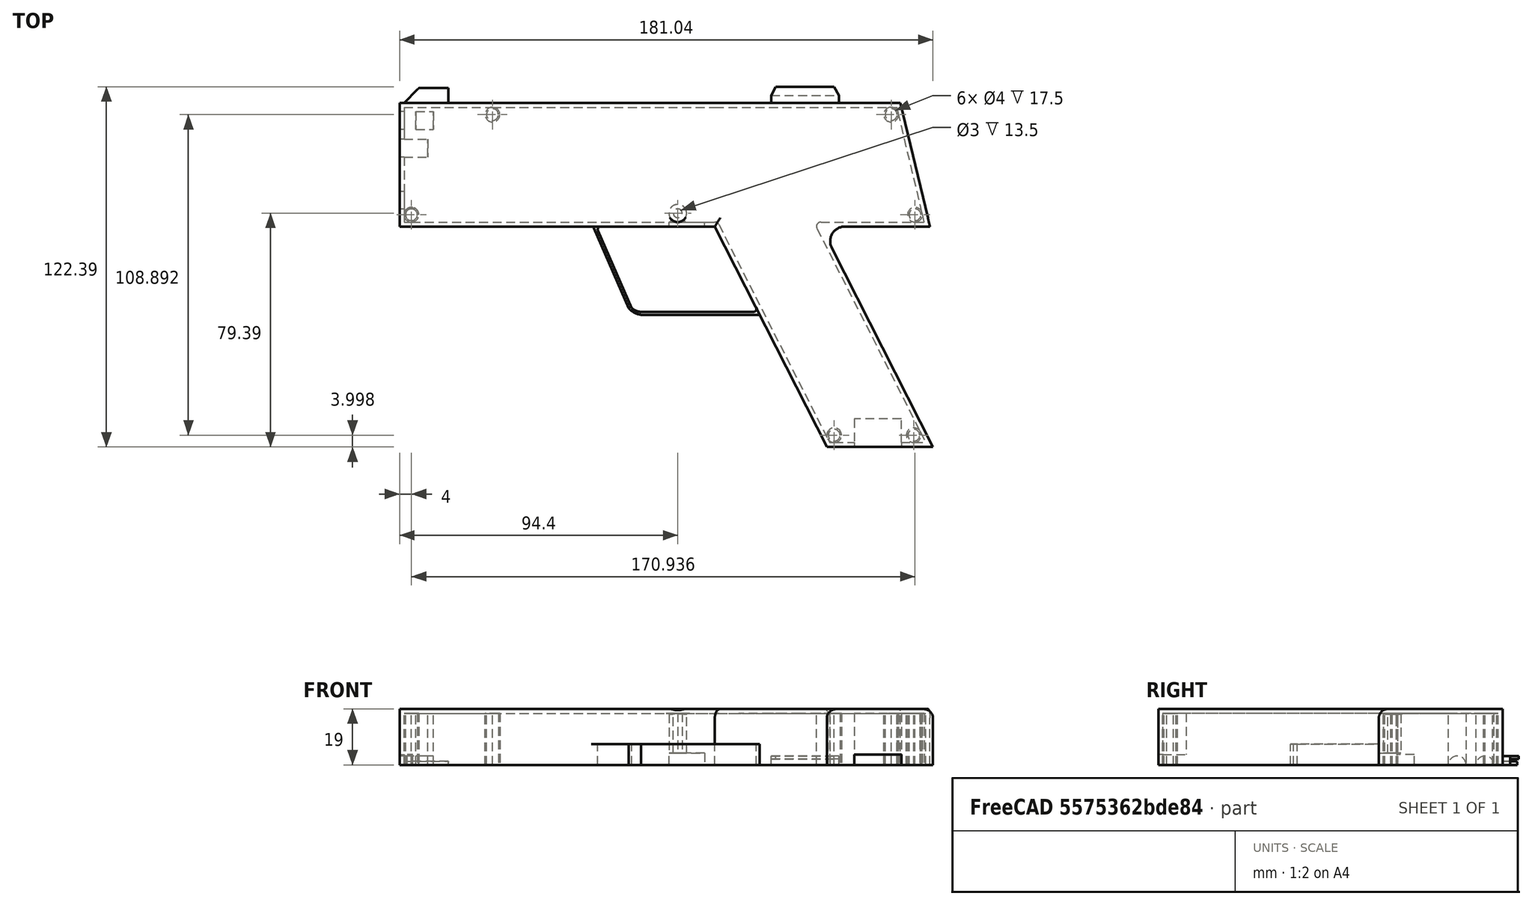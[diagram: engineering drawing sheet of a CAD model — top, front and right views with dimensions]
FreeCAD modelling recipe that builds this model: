
FCSTD DOCUMENT  (FreeCAD 0.21R33771 (Git))
Label: TaggerPart2
License: All rights reserved
LicenseURL: http://en.wikipedia.org/wiki/All_rights_reserved
objects: Sketcher::SketchObject×19, PartDesign::Pad×12, PartDesign::Fillet×5, PartDesign::Pocket×5, PartDesign::Thickness×1, PartDesign::Hole×1, App::MeasureDistance×1, PartDesign::Body×1, App::Part×1
note: 68 computed .brp shape members not serialized (recipe doc carries the construction recipe); baked Part::Feature solids carry a one-line shape summary decoded from their .brp

FEATURE [Sketcher::SketchObject] Sketch
  FullyConstrained = false
  MapMode = 5
  Support = -> [XY_Plane]
  sketch-geometry (12):
    g0: LineSegment StartX=0 StartY=0 StartZ=0 EndX=107 EndY=0 EndZ=0
    g1: LineSegment StartX=0 StartY=0 StartZ=0 EndX=0 EndY=-42 EndZ=0
    g2: LineSegment StartX=0 StartY=-42 StartZ=0 EndX=107 EndY=-42 EndZ=0
    g3: LineSegment StartX=107 StartY=0 StartZ=0 EndX=107 EndY=-42 EndZ=0
    g4: LineSegment StartX=107 StartY=0 StartZ=0 EndX=170 EndY=0 EndZ=0
    g5: LineSegment StartX=107 StartY=-42 StartZ=0 EndX=143 EndY=-42 EndZ=0
    g6: LineSegment StartX=107 StartY=-42 StartZ=0 EndX=145.042 EndY=-116.892 EndZ=0
    g7: LineSegment StartX=143 StartY=-42 StartZ=0 EndX=181.042 EndY=-116.892 EndZ=0
    g8: LineSegment StartX=145.042 StartY=-116.892 StartZ=0 EndX=181.042 EndY=-116.892 EndZ=0
    g9: LineSegment StartX=143 StartY=-42 StartZ=0 EndX=180 EndY=-42 EndZ=0
    g10: LineSegment StartX=180 StartY=-42 StartZ=0 EndX=170 EndY=0 EndZ=0
    g11: LineSegment StartX=170 StartY=0 StartZ=0 EndX=170 EndY=-42 EndZ=0
  constraints (32):
    c: Coincident(g0,g-1)
    c: PointOnObject(g0,g-1)
    c: Coincident(g1,g0)
    c: PointOnObject(g1,g-2)
    c: Coincident(g2,g1)
    c: Horizontal(g2)
    c: Coincident(g3,g0)
    c: Coincident(g3,g2)
    c: Vertical(g3)
    c: Coincident(g4,g0)
    c: PointOnObject(g4,g-1)
    c: Coincident(g5,g2)
    c: Horizontal(g5)
    c: Coincident(g6,g2)
    c: Coincident(g7,g5)
    c: Coincident(g8,g6)
    c: Coincident(g8,g7)
    c: Horizontal(g8)
    c: Coincident(g9,g7)
    c: Horizontal(g9)
    c: Coincident(g10,g9)
    c: Coincident(g10,g4)
    c: Coincident(g11,g4)
    c: PointOnObject(g11,g9)
    c: Vertical(g11)
    c: DistanceY(g1,g1) = 42
    c: DistanceX(g1,g9) = 180
    c: DistanceX(g0,g4) = 170
    c: Parallel(g7,g6)
    c: Distance(g7) = 84
    c: DistanceX(g5,g5) = 36
    c: DistanceX(g9,g9) = 37
FEATURE [Sketcher::SketchObject] Sketch001  label="Triggerumrahmung"
  ExternalGeometry = -> [Sketch]
  FullyConstrained = false
  MapMode = 5
  Support = -> [XY_Plane]
  sketch-geometry (16):
    g0: LineSegment StartX=107 StartY=-42 StartZ=0 EndX=107 EndY=-71 EndZ=0
    g1: LineSegment StartX=107 StartY=-71 StartZ=0 EndX=121.731 EndY=-71 EndZ=0
    g2: LineSegment StartX=107 StartY=-71 StartZ=0 EndX=66.7308 EndY=-71 EndZ=0
    g3: LineSegment StartX=66.7308 StartY=-71 StartZ=0 EndX=66.7308 EndY=-42 EndZ=0
    g4: LineSegment StartX=121.731 StartY=-71 StartZ=0 EndX=81.9929 EndY=-71 EndZ=0
    g5: LineSegment StartX=78.7821 StartY=-69.7248 StartZ=0 EndX=66.7308 EndY=-42 EndZ=0
    g6: ArcOfCircle CenterX=82.1691 CenterY=-65.8766 CenterZ=0 NormalX=0 NormalY=0 NormalZ=1 AngleXU=0 Radius=5.12641 StartAngle=3.99065 EndAngle=4.678
    g7: LineSegment StartX=121.731 StartY=-71 StartZ=0 EndX=121.731 EndY=-72 EndZ=0
    g8: LineSegment StartX=121.731 StartY=-72 StartZ=0 EndX=81.9929 EndY=-72 EndZ=0
    g9: LineSegment StartX=81.9929 StartY=-71 StartZ=0 EndX=81.9929 EndY=-72 EndZ=0
    g10: ArcOfCircle CenterX=82.7291 CenterY=-65.6034 CenterZ=0 NormalX=0 NormalY=0 NormalZ=1 AngleXU=0 Radius=6.43882 StartAngle=3.8362 EndAngle=4.59779
    g11: LineSegment StartX=66.7308 StartY=-42 StartZ=0 EndX=65.7308 EndY=-42 EndZ=0
    g12: LineSegment StartX=65.7308 StartY=-42 StartZ=0 EndX=77.7821 EndY=-69.7248 EndZ=0
    g13: LineSegment StartX=78.7821 StartY=-69.7248 StartZ=0 EndX=77.7821 EndY=-69.7248 EndZ=0
    g14: LineSegment StartX=121.731 StartY=-72 StartZ=0 EndX=122.239 EndY=-72 EndZ=0
    g15: LineSegment StartX=122.239 StartY=-72 StartZ=0 EndX=121.731 EndY=-71 EndZ=0
  constraints (44):
    c: Coincident(g0,g-4)
    c: Vertical(g0)
    c: DistanceY(g0,g0) = 29
    c: PointOnObject(g1,g-3)
    c: Horizontal(g1)
    c: Coincident(g1,g0)
    c: Coincident(g2,g0)
    c: Horizontal(g2)
    c: DistanceX(g2,g1) = 55
    c: Coincident(g3,g2)
    c: PointOnObject(g3,g-4)
    c: Vertical(g3)
    c: Coincident(g4,g1)
    c: Coincident(g5,g3)
    c: Horizontal(g4)
    c: Coincident(g6,g5)
    c: Coincident(g6,g4)
    c: Coincident(g7,g4)
    c: Vertical(g7)
    c: Coincident(g8,g7)
    c: Horizontal(g8)
    c: Coincident(g9,g4)
    c: Coincident(g9,g8)
    c: Vertical(g9)
    c: DistanceY(g9,g9) = 1
    c: Coincident(g10,g8)
    c: Coincident(g11,g5)
    c: PointOnObject(g11,g-4)
    c: DistanceX(g11,g11) = 1
    c: Coincident(g12,g11)
    c: Coincident(g12,g10)
    c: DistanceX(g6) = 82.1691
    c: DistanceY(g6) = -65.8766
    c: Equal(g12,g5)
    c: Coincident(g13,g5)
    c: Horizontal(g13)
    c: Coincident(g10,g13)
    c: DistanceX(g4) = 81.9929
    c: DistanceX(g5) = 78.7821
    c: Coincident(g14,g8)
    c: PointOnObject(g14,g-3)
    c: Horizontal(g14)
    c: Coincident(g15,g14)
    c: Coincident(g15,g4)
FEATURE [Sketcher::SketchObject] Sketch002  label="Kim2"
  AttachmentOffset = pos=(0,0,2) rot=(0,0,1;0rad)
  ExternalGeometry = -> [Sketch]
  FullyConstrained = false
  MapMode = 5
  Placement = pos=(0,0,2) rot=(0,0,1;0rad)
  Support = -> [XY_Plane]
  sketch-geometry (10):
    g0: LineSegment StartX=170 StartY=0 StartZ=0 EndX=170 EndY=-42 EndZ=0
    g1: LineSegment StartX=149.115 StartY=0 StartZ=0 EndX=149.115 EndY=2.5 EndZ=0
    g2: LineSegment StartX=149.115 StartY=2.5 StartZ=0 EndX=147.523 EndY=5.5 EndZ=0
    g3: LineSegment StartX=147.523 StartY=5.5 StartZ=0 EndX=127.662 EndY=5.5 EndZ=0
    g4: LineSegment StartX=127.662 StartY=5.5 StartZ=0 EndX=126.07 EndY=2.5 EndZ=0
    g5: LineSegment StartX=126.07 StartY=2.5 StartZ=0 EndX=126.07 EndY=0 EndZ=0
    g6: LineSegment StartX=126.07 StartY=2.5 StartZ=0 EndX=149.115 EndY=2.5 EndZ=0
    g7: LineSegment StartX=127.662 StartY=5.5 StartZ=0 EndX=127.662 EndY=2.5 EndZ=0
    g8: LineSegment StartX=147.523 StartY=5.5 StartZ=0 EndX=147.523 EndY=2.5 EndZ=0
    g9: LineSegment StartX=126.07 StartY=0 StartZ=0 EndX=149.115 EndY=0 EndZ=0
  constraints (26):
    c: Coincident(g0,g-6)
    c: PointOnObject(g0,g-7)
    c: Vertical(g0)
    c: PointOnObject(g1,g-4)
    c: Vertical(g1)
    c: Coincident(g3,g2)
    c: Horizontal(g3)
    c: Coincident(g4,g3)
    c: Coincident(g5,g4)
    c: PointOnObject(g5,g-4)
    c: Equal(g5,g1)
    c: Equal(g4,g2)
    c: Coincident(g2,g1)
    c: Vertical(g5)
    c: Coincident(g6,g4)
    c: Coincident(g6,g1)
    c: Coincident(g7,g3)
    c: PointOnObject(g7,g6)
    c: Vertical(g7)
    c: Coincident(g8,g2)
    c: PointOnObject(g8,g6)
    c: Vertical(g8)
    c: DistanceY(g8,g8) = 3
    c: DistanceY(g5,g3) = 5.5
    c: Coincident(g9,g5)
    c: Coincident(g9,g1)
FEATURE [Sketcher::SketchObject] Sketch003  label="Korn"
  ExternalGeometry = -> [Sketch,Sketch002]
  FullyConstrained = false
  MapMode = 5
  Support = -> [XY_Plane]
  sketch-geometry (7):
    g0: LineSegment StartX=1.52333 StartY=0 StartZ=0 EndX=6.52333 EndY=5 EndZ=0
    g1: LineSegment StartX=6.52333 StartY=5 StartZ=0 EndX=16.5233 EndY=5 EndZ=0
    g2: LineSegment StartX=16.5233 StartY=5 StartZ=0 EndX=16.5233 EndY=0 EndZ=0
    g3: LineSegment StartX=16.5233 StartY=0 StartZ=0 EndX=1.52333 EndY=0 EndZ=0
    g4: LineSegment StartX=127.662 StartY=5.5 StartZ=0 EndX=127.662 EndY=0 EndZ=0
    g5: LineSegment StartX=6.52333 StartY=5 StartZ=0 EndX=6.52333 EndY=0 EndZ=0
    g6: LineSegment StartX=1.52333 StartY=0 StartZ=0 EndX=1.52333 EndY=-1.50251 EndZ=0
  constraints (19):
    c: Coincident(g1,g0)
    c: Horizontal(g1)
    c: Coincident(g2,g1)
    c: PointOnObject(g2,g-3)
    c: Coincident(g3,g2)
    c: Coincident(g3,g0)
    c: Vertical(g2)
    c: Coincident(g4,g-6)
    c: PointOnObject(g4,g-8)
    c: Vertical(g4)
    c: DistanceY(g2,g2) = 5
    c: Coincident(g5,g0)
    c: PointOnObject(g5,g3)
    c: Vertical(g5)
    c: Angle(g0,g5) = 0.785398
    c: DistanceX(g3,g3) = 15
    c: PointOnObject(g0,g-3)
    c: Coincident(g6,g0)
    c: Vertical(g6)
FEATURE [PartDesign::Pad] Pad
  Direction = (0,0,1)
  Length = 19
  Length2 = 10
  Profile = -> Sketch
  ReferenceAxis = -> Sketch [N_Axis]
  Type = 0
FEATURE [PartDesign::Thickness] Thickness
  Base = -> Pad [Face10]
  BaseFeature = -> Pad
  Intersection = false
  Join = 0
  Mode = 0
  Reversed = true
  SupportTransform = false
  Value = 1.5
FEATURE [Sketcher::SketchObject] Sketch004  label="Kim1"
  ExternalGeometry = -> [Sketch002]
  FullyConstrained = true
  MapMode = 5
  Support = -> [XY_Plane]
  sketch-geometry (4):
    g0: LineSegment StartX=126.07 StartY=2.5 StartZ=0 EndX=149.115 EndY=2.5 EndZ=0
    g1: LineSegment StartX=149.115 StartY=2.5 StartZ=0 EndX=149.115 EndY=0 EndZ=0
    g2: LineSegment StartX=149.115 StartY=0 StartZ=0 EndX=126.07 EndY=0 EndZ=0
    g3: LineSegment StartX=126.07 StartY=0 StartZ=0 EndX=126.07 EndY=2.5 EndZ=0
  constraints (8):
    c: Coincident(g0,g-5)
    c: Coincident(g0,g-7)
    c: Coincident(g1,g0)
    c: Coincident(g1,g-8)
    c: Coincident(g2,g-8)
    c: Coincident(g3,g0)
    c: Coincident(g2,g1)
    c: Coincident(g3,g2)
FEATURE [PartDesign::Pad] Pad001
  BaseFeature = -> Thickness
  Direction = (0,0,1)
  Length = 2
  Length2 = 10
  Profile = -> Sketch004
  ReferenceAxis = -> Sketch004 [N_Axis]
  Type = 0
FEATURE [PartDesign::Pad] Pad002
  BaseFeature = -> Pad001
  Direction = (0,0,1)
  Length = 1
  Length2 = 10
  Profile = -> Sketch002
  ReferenceAxis = -> Sketch002 [N_Axis]
  Type = 0
FEATURE [PartDesign::Pad] Pad003
  BaseFeature = -> Pad002
  Direction = (0,0,1)
  Length = 1.2
  Length2 = 10
  Profile = -> Sketch003
  ReferenceAxis = -> Sketch003 [N_Axis]
  Type = 0
FEATURE [PartDesign::Fillet] Fillet
  Base = -> Pad003 [Edge93]
  BaseFeature = -> Pad003
  Radius = 0.5
  SupportTransform = false
  UseAllEdges = false
FEATURE [PartDesign::Pad] Pad004
  BaseFeature = -> Fillet
  Direction = (0,0,1)
  Length = 7
  Length2 = 10
  Profile = -> Sketch001
  ReferenceAxis = -> Sketch001 [N_Axis]
  Type = 0
FEATURE [Sketcher::SketchObject] Sketch005  label="laserlöcher"
  ExternalGeometry = -> [Pad004]
  FullyConstrained = true
  MapMode = 5
  Placement = pos=(1.5,0,0) rot=(0.57735,0.57735,0.57735;2.0944rad)
  Support = -> [Pad004]
  sketch-geometry (6):
    g0: LineSegment StartX=-12.3 StartY=0 StartZ=0 EndX=0 EndY=0 EndZ=0
    g1: ArcOfCircle CenterX=-15.4 CenterY=0 CenterZ=0 NormalX=0 NormalY=0 NormalZ=1 AngleXU=0 Radius=3.1 StartAngle=0 EndAngle=3.14159
    g2: LineSegment StartX=-18.5 StartY=0 StartZ=0 EndX=-12.3 EndY=0 EndZ=0
    g3: ArcOfCircle CenterX=-6 CenterY=0 CenterZ=0 NormalX=0 NormalY=0 NormalZ=1 AngleXU=0 Radius=3.3 StartAngle=0 EndAngle=3.14159
    g4: LineSegment StartX=-9.3 StartY=0 StartZ=0 EndX=-2.7 EndY=0 EndZ=0
    g5: LineSegment StartX=-40.5 StartY=0 StartZ=0 EndX=-18.5 EndY=0 EndZ=0
  constraints (18):
    c: Radius(g1) = 3.1
    c: Coincident(g2,g1)
    c: Coincident(g2,g1)
    c: Coincident(g0,g-1)
    c: PointOnObject(g3,g0)
    c: PointOnObject(g3,g0)
    c: PointOnObject(g3,g0)
    c: Radius(g3) = 3.3
    c: Coincident(g4,g3)
    c: Coincident(g4,g3)
    c: DistanceX(g1,g3) = 3
    c: Coincident(g5,g-3)
    c: Coincident(g5,g1)
    c: Horizontal(g5)
    c: DistanceX(g5,g5) = 22
    c: Coincident(g0,g1)
    c: Horizontal(g0)
    c: PointOnObject(g1,g2)
FEATURE [Sketcher::SketchObject] Sketch006  label="Schraubenlöcher"
  ExternalGeometry = -> [Pad004]
  FullyConstrained = false
  MapMode = 5
  Placement = pos=(0,0,17.5) rot=(1,0,0;3.14159rad)
  Support = -> [Pad004]
  sketch-geometry (20):
    g0: Circle CenterX=31.5 CenterY=4 CenterZ=0 NormalX=0 NormalY=0 NormalZ=1 AngleXU=0 Radius=2
    g1: Circle CenterX=31.5 CenterY=4 CenterZ=0 NormalX=0 NormalY=0 NormalZ=1 AngleXU=0 Radius=2.5
    g2: Circle CenterX=4 CenterY=38 CenterZ=0 NormalX=0 NormalY=0 NormalZ=1 AngleXU=0 Radius=2.5
    g3: Circle CenterX=4 CenterY=38 CenterZ=0 NormalX=0 NormalY=0 NormalZ=1 AngleXU=0 Radius=2
    g4: Circle CenterX=147.497 CenterY=112.892 CenterZ=0 NormalX=0 NormalY=0 NormalZ=1 AngleXU=0 Radius=2
    g5: Circle CenterX=147.497 CenterY=112.892 CenterZ=0 NormalX=0 NormalY=0 NormalZ=1 AngleXU=0 Radius=2.5
    g6: Circle CenterX=166.841 CenterY=4 CenterZ=0 NormalX=0 NormalY=0 NormalZ=1 AngleXU=0 Radius=2
    g7: Circle CenterX=166.841 CenterY=4 CenterZ=0 NormalX=0 NormalY=0 NormalZ=1 AngleXU=0 Radius=2.5
    g8: Circle CenterX=174.524 CenterY=112.892 CenterZ=0 NormalX=0 NormalY=0 NormalZ=1 AngleXU=0 Radius=2
    g9: Circle CenterX=174.524 CenterY=112.892 CenterZ=0 NormalX=0 NormalY=0 NormalZ=1 AngleXU=0 Radius=2.5
    g10: Circle CenterX=174.936 CenterY=38 CenterZ=0 NormalX=0 NormalY=0 NormalZ=1 AngleXU=0 Radius=2
    g11: Circle CenterX=174.936 CenterY=38 CenterZ=0 NormalX=0 NormalY=0 NormalZ=1 AngleXU=0 Radius=2.5
    g12: GeomPoint X=166.841 Y=1.5 Z=0
    g13: GeomPoint X=169.273 Y=3.42095 Z=0
    g14: GeomPoint X=174.936 Y=40.5 Z=0
    g15: GeomPoint X=177.368 Y=37.4209 Z=0
    g16: GeomPoint X=147.497 Y=115.392 Z=0
    g17: GeomPoint X=145.268 Y=114.024 Z=0
    g18: GeomPoint X=31.5 Y=1.5 Z=0
    g19: GeomPoint X=1.5 Y=3.78568 Z=0
  constraints (39):
    c: Coincident(g1,g0)
    c: Coincident(g3,g2)
    c: Equal(g3,g0)
    c: Tangent(g-5,g2)
    c: Tangent(g2,g-6)
    c: Radius(g2) = 2.5
    c: Radius(g3) = 2
    c: Coincident(g5,g4)
    c: Radius(g5) = 2.5
    c: Radius(g4) = 2
    c: Coincident(g7,g6)
    c: Radius(g6) = 2
    c: Coincident(g9,g8)
    c: Radius(g8) = 2
    c: Radius(g9) = 2.5
    c: Tangent(g9,g-8)
    c: Tangent(g9,g-7)
    c: Coincident(g11,g10)
    c: Radius(g11) = 2.5
    c: Radius(g7) = 2.5
    c: PointOnObject(g12,g7)
    c: PointOnObject(g13,g7)
    c: PointOnObject(g12,g-9)
    c: PointOnObject(g13,g-3)
    c: Radius(g10) = 2
    c: PointOnObject(g14,g11)
    c: PointOnObject(g15,g11)
    c: PointOnObject(g14,g-10)
    c: PointOnObject(g15,g-3)
    c: Radius(g1) = 2.5
    c: PointOnObject(g16,g5)
    c: PointOnObject(g17,g5)
    c: PointOnObject(g16,g-8)
    c: PointOnObject(g17,g-11)
    c: PointOnObject(g18,g1)
    c: PointOnObject(g18,g-4)
    c: DistanceX(g-6,g-6) = 0
    c: PointOnObject(g19,g-6)
    c: DistanceX(g19,g0) = 30
FEATURE [PartDesign::Pad] Pad005
  BaseFeature = -> Pad004
  Direction = (0,0,-1)
  Length = 17.5
  Length2 = 10
  Profile = -> Sketch006
  ReferenceAxis = -> Sketch006 [N_Axis]
  Type = 0
FEATURE [Sketcher::SketchObject] Sketch007  label="Triggerausschnitt"
  ExternalGeometry = -> [Pad005]
  FullyConstrained = true
  MapMode = 5
  Placement = pos=(0,-42,0) rot=(1,0,0;1.5708rad)
  Support = -> [Pad005]
  sketch-geometry (4):
    g0: LineSegment StartX=103.5 StartY=0 StartZ=0 EndX=103.5 EndY=4 EndZ=0
    g1: LineSegment StartX=103.5 StartY=4 StartZ=0 EndX=91.5 EndY=4 EndZ=0
    g2: LineSegment StartX=91.5 StartY=4 StartZ=0 EndX=91.5 EndY=0 EndZ=0
    g3: LineSegment StartX=91.5 StartY=0 StartZ=0 EndX=103.5 EndY=0 EndZ=0
  constraints (12):
    c: PointOnObject(g0,g-3)
    c: Vertical(g0)
    c: Coincident(g1,g0)
    c: Horizontal(g1)
    c: Coincident(g2,g1)
    c: PointOnObject(g2,g-3)
    c: Vertical(g2)
    c: DistanceY(g2,g2) = 4
    c: Coincident(g3,g2)
    c: Coincident(g3,g0)
    c: DistanceX(g1,g0) = 12
    c: DistanceX(g0,g-3) = 3.5
FEATURE [PartDesign::Pocket] Pocket
  BaseFeature = -> Pad005
  Direction = (0,1,-2e-16)
  Length = 5
  Length2 = 5
  Profile = -> Sketch007
  ReferenceAxis = -> Sketch007 [N_Axis]
  Type = 0
FEATURE [PartDesign::Hole] Hole
  BaseFeature = -> Pocket
  CustomThreadClearance = 0
  Depth = 25
  DepthType = 0
  Diameter = 6
  DrillForDepth = false
  DrillPoint = 1
  DrillPointAngle = 118
  HoleCutCountersinkAngle = 90
  HoleCutCustomValues = false
  HoleCutDepth = 0
  HoleCutDiameter = 6.1
  HoleCutType = 0
  ModelThread = false
  Profile = -> Sketch005
  Tapered = false
  TaperedAngle = 90
  ThreadClass = 0
  ThreadDepth = 25
  ThreadDepthType = 0
  ThreadDirection = 0
  ThreadFit = 0
  ThreadSize = 0
  ThreadType = 0
  Threaded = false
  UseCustomThreadClearance = false
FEATURE [Sketcher::SketchObject] Sketch010  label="Datenkabelloch"
  FullyConstrained = false
  MapMode = 5
  Placement = pos=(0,-115.392,0) rot=(0,0.707107,0.707107;3.14159rad)
  sketch-geometry (10):
    g0: LineSegment StartX=-178.598 StartY=11.5 StartZ=0 EndX=-174.524 EndY=11.5 EndZ=0
    g1: LineSegment StartX=-147.497 StartY=11.5 StartZ=0 EndX=-145.963 EndY=11.5 EndZ=0
    g2: LineSegment StartX=-178.598 StartY=0 StartZ=0 EndX=-162.28 EndY=0 EndZ=0
    g3: LineSegment StartX=-162.28 StartY=0 StartZ=0 EndX=-145.963 EndY=0 EndZ=0
    g4: LineSegment StartX=-162.28 StartY=0 StartZ=0 EndX=-162.28 EndY=3.5 EndZ=0
    g5: LineSegment StartX=-162.28 StartY=3.5 StartZ=0 EndX=-154.28 EndY=3.5 EndZ=0
    g6: LineSegment StartX=-162.28 StartY=3.5 StartZ=0 EndX=-170.28 EndY=3.5 EndZ=0
    g7: LineSegment StartX=-170.28 StartY=3.5 StartZ=0 EndX=-170.28 EndY=3.73e-14 EndZ=0
    g8: LineSegment StartX=-154.28 StartY=3.5 StartZ=0 EndX=-154.28 EndY=-3.86e-14 EndZ=0
    g9: LineSegment StartX=-154.28 StartY=-3.86e-14 StartZ=0 EndX=-170.28 EndY=3.74e-14 EndZ=0
  constraints (19):
    c: Coincident(g3,g2)
    c: Equal(g2,g3)
    c: Coincident(g4,g2)
    c: Vertical(g4)
    c: DistanceY(g4,g4) = 3.5
    c: Coincident(g5,g4)
    c: Horizontal(g5)
    c: Coincident(g6,g5)
    c: Equal(g6,g5)
    c: Horizontal(g6)
    c: DistanceX(g5,g5) = 8
    c: Coincident(g7,g6)
    c: PointOnObject(g7,g2)
    c: Vertical(g7)
    c: Coincident(g8,g5)
    c: PointOnObject(g8,g3)
    c: Vertical(g8)
    c: Coincident(g9,g8)
    c: Coincident(g9,g7)
FEATURE [PartDesign::Pocket] Pocket001
  BaseFeature = -> Hole
  Direction = (0,-1,2e-16)
  Length = 5
  Length2 = 5
  Profile = -> Sketch010
  ReferenceAxis = -> Sketch010 [N_Axis]
  Type = 0
FEATURE [Sketcher::SketchObject] Sketch011  label="Lautsprecherbefestigung"
  ExternalGeometry = -> [Pocket001]
  FullyConstrained = false
  MapMode = 5
  Placement = pos=(0,0,17.5) rot=(1,0,0;3.14159rad)
  Support = -> [Pocket001]
  sketch-geometry (7):
    g0: Circle CenterX=131.056 CenterY=21.3061 CenterZ=0 NormalX=0 NormalY=0 NormalZ=1 AngleXU=0 Radius=15.5
    g1: Circle CenterX=131.056 CenterY=21.3061 CenterZ=0 NormalX=0 NormalY=0 NormalZ=1 AngleXU=0 Radius=16
    g2: LineSegment StartX=131.056 StartY=21.3061 StartZ=0 EndX=131.056 EndY=1.5 EndZ=0
    g3: LineSegment StartX=131.056 StartY=21.3061 StartZ=0 EndX=143 EndY=40.5 EndZ=0
    g4: LineSegment StartX=143 StartY=42 StartZ=0 EndX=131.056 EndY=21.3061 EndZ=0
    g5: LineSegment StartX=141.678 StartY=42.7087 StartZ=0 EndX=131.056 EndY=21.3061 EndZ=0
    g6: LineSegment StartX=131.056 StartY=21.3061 StartZ=0 EndX=147.497 EndY=112.892 EndZ=0
  constraints (14):
    c: Coincident(g1,g0)
    c: Radius(g1) = 16
    c: Radius(g0) = 15.5
    c: Coincident(g2,g0)
    c: PointOnObject(g2,g-3)
    c: Vertical(g2)
    c: Coincident(g3,g0)
    c: Coincident(g3,g-8)
    c: Coincident(g4,g0)
    c: Coincident(g5,g0)
    c: Equal(g5,g4)
    c: Coincident(g6,g0)
    c: DistanceX(g0) = 131.056
    c: DistanceY(g0) = 21.3061
FEATURE [Sketcher::SketchObject] Sketch012  label="Lautsprecherbefestigung-optimierungen"
  ExternalGeometry = -> [Sketch011]
  FullyConstrained = true
  MapMode = 5
  Placement = pos=(0,0,17.5) rot=(1,0,0;3.14159rad)
  Support = -> [Pocket001]
  sketch-geometry (21):
    g0: ArcOfCircle CenterX=131.056 CenterY=21.3061 CenterZ=0 NormalX=0 NormalY=0 NormalZ=1 AngleXU=0 Radius=15.5 StartAngle=1.24234 EndAngle=1.89925
    g1: LineSegment StartX=126.056 StartY=35.9775 StartZ=0 EndX=131.056 EndY=35.9775 EndZ=0
    g2: LineSegment StartX=131.056 StartY=35.9775 StartZ=0 EndX=136.056 EndY=35.9775 EndZ=0
    g3: LineSegment StartX=131.056 StartY=35.9775 StartZ=0 EndX=131.056 EndY=21.3061 EndZ=0
    g4: LineSegment StartX=126.056 StartY=35.9775 StartZ=0 EndX=126.056 EndY=36.5048 EndZ=0
    g5: LineSegment StartX=136.056 StartY=35.9775 StartZ=0 EndX=136.056 EndY=36.5048 EndZ=0
    g6: ArcOfCircle CenterX=131.056 CenterY=21.3061 CenterZ=0 NormalX=0 NormalY=0 NormalZ=1 AngleXU=0 Radius=16 StartAngle=1.25297 EndAngle=1.88862
    g7: ArcOfCircle CenterX=131.056 CenterY=21.3061 CenterZ=0 NormalX=0 NormalY=0 NormalZ=1 AngleXU=0 Radius=15.5 StartAngle=4.38393 EndAngle=5.04084
    g8: LineSegment StartX=126.056 StartY=6.63469 StartZ=0 EndX=131.056 EndY=6.63469 EndZ=0
    g9: LineSegment StartX=131.056 StartY=6.63469 StartZ=0 EndX=136.056 EndY=6.63469 EndZ=0
    g10: LineSegment StartX=126.056 StartY=6.63469 StartZ=0 EndX=126.056 EndY=6.10741 EndZ=0
    g11: LineSegment StartX=136.056 StartY=6.63469 StartZ=0 EndX=136.056 EndY=6.10741 EndZ=0
    g12: ArcOfCircle CenterX=131.056 CenterY=21.3061 CenterZ=0 NormalX=0 NormalY=0 NormalZ=1 AngleXU=0 Radius=16 StartAngle=4.39457 EndAngle=5.03021
    g13: LineSegment StartX=131.056 StartY=6.63469 StartZ=0 EndX=131.056 EndY=21.3061 EndZ=0
    g14: ArcOfCircle CenterX=131.056 CenterY=21.3061 CenterZ=0 NormalX=0 NormalY=0 NormalZ=1 AngleXU=0 Radius=15.5 StartAngle=3.05115 EndAngle=3.23204
    g15: LineSegment StartX=115.619 StartY=22.7061 StartZ=0 EndX=115.619 EndY=21.3061 EndZ=0
    g16: LineSegment StartX=115.619 StartY=21.3061 StartZ=0 EndX=115.619 EndY=19.9061 EndZ=0
    g17: LineSegment StartX=115.619 StartY=21.3061 StartZ=0 EndX=131.056 EndY=21.3061 EndZ=0
    g18: LineSegment StartX=115.619 StartY=22.7061 StartZ=0 EndX=115.117 EndY=22.7061 EndZ=0
    g19: LineSegment StartX=115.619 StartY=19.9061 StartZ=0 EndX=115.117 EndY=19.9061 EndZ=0
    g20: ArcOfCircle CenterX=131.056 CenterY=21.3061 CenterZ=0 NormalX=0 NormalY=0 NormalZ=1 AngleXU=0 Radius=16 StartAngle=3.05398 EndAngle=3.2292
  constraints (57):
    c: Coincident(g6,g5)
    c: Coincident(g0,g5)
    c: Vertical(g5)
    c: Vertical(g4)
    c: Coincident(g6,g4)
    c: Coincident(g4,g0)
    c: Coincident(g2,g1)
    c: Coincident(g1,g3)
    c: Horizontal(g1)
    c: Horizontal(g2)
    c: Vertical(g3)
    c: DistanceX(g2,g2) = 5
    c: Coincident(g1,g0)
    c: PointOnObject(g5,g-3)
    c: Coincident(g6,g-4)
    c: Coincident(g6,g3)
    c: Coincident(g6,g0)
    c: Coincident(g0,g2)
    c: PointOnObject(g0,g-4)
    c: Coincident(g7,g0)
    c: PointOnObject(g7,g-4)
    c: Coincident(g8,g7)
    c: Horizontal(g8)
    c: Coincident(g9,g8)
    c: Coincident(g9,g7)
    c: Horizontal(g9)
    c: Equal(g9,g8)
    c: DistanceX(g8,g8) = 5
    c: Coincident(g10,g7)
    c: PointOnObject(g10,g-3)
    c: Vertical(g10)
    c: Coincident(g11,g7)
    c: Coincident(g12,g0)
    c: Coincident(g12,g10)
    c: Coincident(g12,g11)
    c: Coincident(g13,g8)
    c: Coincident(g13,g0)
    c: Coincident(g14,g0)
    c: PointOnObject(g14,g-4)
    c: Coincident(g15,g14)
    c: Vertical(g15)
    c: Coincident(g16,g15)
    c: Coincident(g16,g14)
    c: Vertical(g16)
    c: Vertical(g11)
    c: Equal(g16,g15)
    c: Coincident(g17,g15)
    c: Coincident(g17,g0)
    c: Coincident(g18,g14)
    c: PointOnObject(g18,g-3)
    c: Horizontal(g18)
    c: Coincident(g19,g14)
    c: Horizontal(g19)
    c: Coincident(g20,g0)
    c: Coincident(g20,g19)
    c: Coincident(g20,g18)
    c: DistanceY(g15,g15) = 1.4
FEATURE [Sketcher::SketchObject] Sketch013  label="Sechsecke-Loch"
  ExternalGeometry = -> [Sketch011,Sketch012]
  FullyConstrained = true
  MapMode = 5
  Placement = pos=(0,0,17.5) rot=(1,0,0;3.14159rad)
  Support = -> [Pocket001]
  sketch-geometry (65):
    g0: LineSegment StartX=131.056 StartY=21.3061 StartZ=0 EndX=131.056 EndY=23.3061 EndZ=0
    g1: LineSegment StartX=131.056 StartY=21.3061 StartZ=0 EndX=131.056 EndY=19.3061 EndZ=0
    g2: LineSegment StartX=131.056 StartY=23.3061 StartZ=0 EndX=132.21 EndY=23.3061 EndZ=0
    g3: LineSegment StartX=131.056 StartY=23.3061 StartZ=0 EndX=129.901 EndY=23.3061 EndZ=0
    g4: LineSegment StartX=129.901 StartY=23.3061 StartZ=0 EndX=128.746 EndY=21.3061 EndZ=0
    g5: LineSegment StartX=131.056 StartY=19.3061 StartZ=0 EndX=132.21 EndY=19.3061 EndZ=0
    g6: LineSegment StartX=131.056 StartY=19.3061 StartZ=0 EndX=129.901 EndY=19.3061 EndZ=0
    g7: LineSegment StartX=129.901 StartY=19.3061 StartZ=0 EndX=128.746 EndY=21.3061 EndZ=0
    g8: LineSegment StartX=132.21 StartY=19.3061 StartZ=0 EndX=133.365 EndY=21.3061 EndZ=0
    g9: LineSegment StartX=133.365 StartY=21.3061 StartZ=0 EndX=132.21 EndY=23.3061 EndZ=0
    g10: LineSegment StartX=129.901 StartY=19.3061 StartZ=0 EndX=132.21 EndY=19.3061 EndZ=0
    g11: LineSegment StartX=129.901 StartY=19.3061 StartZ=0 EndX=129.151 EndY=18.0071 EndZ=0
    g12: LineSegment StartX=132.21 StartY=19.3061 StartZ=0 EndX=132.96 EndY=18.0071 EndZ=0
    g13: LineSegment StartX=133.365 StartY=21.3061 StartZ=0 EndX=134.865 EndY=21.3061 EndZ=0
    g14: LineSegment StartX=132.21 StartY=23.3061 StartZ=0 EndX=132.96 EndY=24.6051 EndZ=0
    g15: LineSegment StartX=129.901 StartY=23.3061 StartZ=0 EndX=129.151 EndY=24.6051 EndZ=0
    g16: LineSegment StartX=128.746 StartY=21.3061 StartZ=0 EndX=127.246 EndY=21.3061 EndZ=0
    g17: LineSegment StartX=132.96 StartY=18.0071 StartZ=0 EndX=132.21 EndY=18.0071 EndZ=0
    g18: LineSegment StartX=129.151 StartY=18.0071 StartZ=0 EndX=129.901 EndY=18.0071 EndZ=0
    g19: LineSegment StartX=129.901 StartY=18.0071 StartZ=0 EndX=132.21 EndY=18.0071 EndZ=0
    g20: LineSegment StartX=129.901 StartY=18.0071 StartZ=0 EndX=128.746 EndY=16.0071 EndZ=0
    g21: LineSegment StartX=128.746 StartY=16.0071 StartZ=0 EndX=129.901 EndY=14.0071 EndZ=0
    g22: LineSegment StartX=129.901 StartY=14.0071 StartZ=0 EndX=132.21 EndY=14.0071 EndZ=0
    g23: LineSegment StartX=132.21 StartY=14.0071 StartZ=0 EndX=133.365 EndY=16.0071 EndZ=0
    g24: LineSegment StartX=133.365 StartY=16.0071 StartZ=0 EndX=132.21 EndY=18.0071 EndZ=0
    g25: LineSegment StartX=132.96 StartY=18.0071 StartZ=0 EndX=133.335 EndY=18.6566 EndZ=0
    g26: LineSegment StartX=134.865 StartY=21.3061 StartZ=0 EndX=134.49 EndY=20.6566 EndZ=0
    g27: LineSegment StartX=134.49 StartY=20.6566 StartZ=0 EndX=133.335 EndY=18.6566 EndZ=0
    g28: LineSegment StartX=134.865 StartY=21.3061 StartZ=0 EndX=134.49 EndY=21.9556 EndZ=0
    g29: LineSegment StartX=132.96 StartY=24.6051 StartZ=0 EndX=133.335 EndY=23.9556 EndZ=0
    g30: LineSegment StartX=133.335 StartY=23.9556 StartZ=0 EndX=134.49 EndY=21.9556 EndZ=0
    g31: LineSegment StartX=129.151 StartY=24.6051 StartZ=0 EndX=129.901 EndY=24.6051 EndZ=0
    g32: LineSegment StartX=132.96 StartY=24.6051 StartZ=0 EndX=132.21 EndY=24.6051 EndZ=0
    g33: LineSegment StartX=129.901 StartY=24.6051 StartZ=0 EndX=132.21 EndY=24.6051 EndZ=0
    g34: LineSegment StartX=129.151 StartY=24.6051 StartZ=0 EndX=128.776 EndY=23.9556 EndZ=0
    g35: LineSegment StartX=127.246 StartY=21.3061 StartZ=0 EndX=127.621 EndY=21.9556 EndZ=0
    g36: LineSegment StartX=128.776 StartY=23.9556 StartZ=0 EndX=127.621 EndY=21.9556 EndZ=0
    g37: LineSegment StartX=133.335 StartY=18.6566 StartZ=0 EndX=134.49 EndY=16.6566 EndZ=0
    g38: LineSegment StartX=134.49 StartY=16.6566 StartZ=0 EndX=136.8 EndY=16.6566 EndZ=0
    g39: LineSegment StartX=136.8 StartY=16.6566 StartZ=0 EndX=137.954 EndY=18.6566 EndZ=0
    g40: LineSegment StartX=137.954 StartY=18.6566 StartZ=0 EndX=136.8 EndY=20.6566 EndZ=0
    g41: LineSegment StartX=136.8 StartY=20.6566 StartZ=0 EndX=134.49 EndY=20.6566 EndZ=0
    g42: LineSegment StartX=134.49 StartY=21.9556 StartZ=0 EndX=136.8 EndY=21.9556 EndZ=0
    g43: LineSegment StartX=136.8 StartY=21.9556 StartZ=0 EndX=137.954 EndY=23.9556 EndZ=0
    g44: LineSegment StartX=137.954 StartY=23.9556 StartZ=0 EndX=136.8 EndY=25.9556 EndZ=0
    g45: LineSegment StartX=136.8 StartY=25.9556 StartZ=0 EndX=134.49 EndY=25.9556 EndZ=0
    g46: LineSegment StartX=134.49 StartY=25.9556 StartZ=0 EndX=133.335 EndY=23.9556 EndZ=0
    g47: LineSegment StartX=132.21 StartY=24.6051 StartZ=0 EndX=133.365 EndY=26.6051 EndZ=0
    g48: LineSegment StartX=133.365 StartY=26.6051 StartZ=0 EndX=132.21 EndY=28.6051 EndZ=0
    g49: LineSegment StartX=132.21 StartY=28.6051 StartZ=0 EndX=129.901 EndY=28.6051 EndZ=0
    g50: LineSegment StartX=129.901 StartY=28.6051 StartZ=0 EndX=128.746 EndY=26.6051 EndZ=0
    g51: LineSegment StartX=128.746 StartY=26.6051 StartZ=0 EndX=129.901 EndY=24.6051 EndZ=0
    g52: LineSegment StartX=127.621 StartY=21.9556 StartZ=0 EndX=125.312 EndY=21.9556 EndZ=0
    g53: LineSegment StartX=125.312 StartY=21.9556 StartZ=0 EndX=124.157 EndY=23.9556 EndZ=0
    g54: LineSegment StartX=124.157 StartY=23.9556 StartZ=0 EndX=125.312 EndY=25.9556 EndZ=0
    g55: LineSegment StartX=125.312 StartY=25.9556 StartZ=0 EndX=127.621 EndY=25.9556 EndZ=0
    g56: LineSegment StartX=127.621 StartY=25.9556 StartZ=0 EndX=128.776 EndY=23.9556 EndZ=0
    g57: LineSegment StartX=127.246 StartY=21.3061 StartZ=0 EndX=127.621 EndY=20.6566 EndZ=0
    g58: LineSegment StartX=129.151 StartY=18.0071 StartZ=0 EndX=128.776 EndY=18.6566 EndZ=0
    g59: LineSegment StartX=127.621 StartY=20.6566 StartZ=0 EndX=128.776 EndY=18.6566 EndZ=0
    g60: LineSegment StartX=128.776 StartY=18.6566 StartZ=0 EndX=127.621 EndY=16.6566 EndZ=0
    g61: LineSegment StartX=127.621 StartY=16.6566 StartZ=0 EndX=125.312 EndY=16.6566 EndZ=0
    g62: LineSegment StartX=125.312 StartY=16.6566 StartZ=0 EndX=124.157 EndY=18.6566 EndZ=0
    g63: LineSegment StartX=124.157 StartY=18.6566 StartZ=0 EndX=125.312 EndY=20.6566 EndZ=0
    g64: LineSegment StartX=125.312 StartY=20.6566 StartZ=0 EndX=127.621 EndY=20.6566 EndZ=0
  constraints (180):
    c: Coincident(g0,g-4)
    c: Vertical(g0)
    c: Coincident(g1,g0)
    c: Vertical(g1)
    c: Equal(g1,g0)
    c: Coincident(g2,g0)
    c: Horizontal(g2)
    c: Coincident(g3,g2)
    c: Horizontal(g3)
    c: Coincident(g4,g3)
    c: Coincident(g5,g1)
    c: Horizontal(g5)
    c: Coincident(g6,g5)
    c: Horizontal(g6)
    c: Coincident(g7,g6)
    c: Coincident(g7,g4)
    c: Coincident(g8,g5)
    c: Coincident(g9,g8)
    c: Coincident(g9,g2)
    c: Equal(g3,g2)
    c: Equal(g2,g6)
    c: Equal(g6,g5)
    c: Equal(g7,g4)
    c: Equal(g4,g9)
    c: Equal(g9,g8)
    c: Coincident(g10,g6)
    c: Coincident(g10,g5)
    c: Equal(g10,g8)
    c: Angle(g4,g3) = 2.0944
    c: Distance(g1) = 2
    c: Coincident(g11,g6)
    c: Coincident(g12,g5)
    c: Coincident(g13,g8)
    c: Horizontal(g13)
    c: Coincident(g14,g2)
    c: Coincident(g15,g3)
    c: Coincident(g16,g4)
    c: Equal(g15,g14)
    c: Equal(g14,g13)
    c: Equal(g13,g12)
    c: Equal(g12,g11)
    c: Distance(g15) = 1.5
    c: Coincident(g17,g12)
    c: Horizontal(g17)
    c: Coincident(g18,g11)
    c: Horizontal(g18)
    c: Coincident(g19,g18)
    c: Coincident(g19,g17)
    c: Horizontal(g19)
    c: Equal(g19,g7)
    c: Equal(g17,g18)
    c: Coincident(g20,g19)
    c: Coincident(g21,g20)
    c: Coincident(g22,g21)
    c: Horizontal(g22)
    c: Coincident(g23,g22)
    c: Coincident(g24,g23)
    c: Coincident(g24,g19)
    c: Equal(g20,g21)
    c: Equal(g21,g22)
    c: Equal(g22,g23)
    c: Equal(g23,g24)
    c: Equal(g24,g19)
    c: Angle(g19,g24) = 2.0944
    c: Angle(g24,g23) = 2.0944
    c: Coincident(g25,g12)
    c: Coincident(g26,g13)
    c: Coincident(g27,g26)
    c: Coincident(g27,g25)
    c: Parallel(g26,g8)
    c: Parallel(g27,g8)
    c: Parallel(g25,g8)
    c: Equal(g27,g8)
    c: Equal(g26,g25)
    c: Coincident(g28,g13)
    c: Coincident(g29,g14)
    c: Coincident(g30,g29)
    c: Coincident(g30,g28)
    c: Parallel(g29,g9)
    c: Parallel(g30,g9)
    c: Parallel(g28,g9)
    c: Equal(g30,g9)
    c: Equal(g28,g29)
    c: Coincident(g31,g15)
    c: Horizontal(g31)
    c: Coincident(g32,g14)
    c: Horizontal(g32)
    c: Coincident(g33,g31)
    c: Coincident(g33,g32)
    c: Horizontal(g33)
    c: Equal(g31,g32)
    c: Equal(g33,g4)
    c: Coincident(g34,g15)
    c: Coincident(g35,g16)
    c: Coincident(g36,g34)
    c: Coincident(g36,g35)
    c: Parallel(g35,g4)
    c: Parallel(g36,g4)
    c: Parallel(g4,g34)
    c: Equal(g34,g35)
    c: Equal(g36,g4)
    c: Coincident(g37,g27)
    c: Coincident(g38,g37)
    c: Horizontal(g38)
    c: Coincident(g39,g38)
    c: Coincident(g40,g39)
    c: Coincident(g41,g40)
    c: Coincident(g41,g27)
    c: Coincident(g42,g30)
    c: Coincident(g43,g42)
    c: Coincident(g44,g43)
    c: Coincident(g45,g44)
    c: Coincident(g46,g45)
    c: Coincident(g46,g30)
    c: Coincident(g47,g33)
    c: Coincident(g48,g47)
    c: Coincident(g49,g48)
    c: Coincident(g50,g49)
    c: Coincident(g51,g50)
    c: Coincident(g51,g33)
    c: Coincident(g52,g36)
    c: Horizontal(g52)
    c: Coincident(g53,g52)
    c: Coincident(g54,g53)
    c: Coincident(g55,g54)
    c: Coincident(g56,g55)
    c: Coincident(g56,g36)
    c: Coincident(g57,g16)
    c: Coincident(g58,g11)
    c: Coincident(g59,g57)
    c: Coincident(g59,g58)
    c: Parallel(g57,g7)
    c: Parallel(g59,g7)
    c: Parallel(g58,g7)
    c: Equal(g58,g57)
    c: Equal(g59,g7)
    c: Coincident(g60,g59)
    c: Coincident(g61,g60)
    c: Coincident(g62,g61)
    c: Coincident(g63,g62)
    c: Coincident(g64,g63)
    c: Coincident(g64,g59)
    c: Horizontal(g64)
    c: Horizontal(g42)
    c: Horizontal(g41)
    c: Equal(g46,g45)
    c: Equal(g45,g44)
    c: Equal(g44,g43)
    c: Equal(g43,g42)
    c: Equal(g42,g41)
    c: Equal(g41,g40)
    c: Equal(g40,g39)
    c: Equal(g39,g37)
    c: Equal(g37,g38)
    c: Equal(g38,g27)
    c: Equal(g27,g47)
    c: Equal(g47,g48)
    c: Equal(g48,g49)
    c: Equal(g49,g50)
    c: Equal(g50,g51)
    c: Equal(g51,g56)
    c: Equal(g56,g55)
    c: Equal(g55,g54)
    c: Equal(g54,g53)
    c: Equal(g53,g52)
    c: Equal(g52,g64)
    c: Equal(g64,g63)
    c: Equal(g63,g62)
    c: Equal(g62,g61)
    c: Equal(g61,g60)
    c: Parallel(g24,g56)
    c: Parallel(g56,g40)
    c: Parallel(g40,g44)
    c: Parallel(g44,g48)
    c: Horizontal(g49)
    c: Horizontal(g55)
    c: Parallel(g63,g46)
    c: Parallel(g46,g60)
    c: Parallel(g43,g47)
    c: Parallel(g47,g36)
FEATURE [PartDesign::Pad] Pad008
  BaseFeature = -> Pocket001
  Direction = (0,0,-1)
  Length = 0.1
  Length2 = 10
  Profile = -> Sketch011
  ReferenceAxis = -> Sketch011 [N_Axis]
  Reversed = true
  Type = 0
FEATURE [PartDesign::Pocket] Pocket002
  BaseFeature = -> Pad008
  Direction = (0,0,1)
  Length = 5
  Length2 = 5
  Profile = -> Sketch012
  ReferenceAxis = -> Sketch012 [N_Axis]
  Reversed = true
  Type = 0
FEATURE [PartDesign::Pocket] Pocket003  label="Lautsprecher_Loch"
  BaseFeature = -> Pocket002
  Direction = (0,0,1)
  Length = 5
  Length2 = 5
  Profile = -> Sketch013
  ReferenceAxis = -> Sketch013 [N_Axis]
  Reversed = true
  Type = 0
FEATURE [Sketcher::SketchObject] Sketch026
  FullyConstrained = false
  MapMode = 5
  Placement = pos=(0,0,17.5) rot=(1,0,0;3.14159rad)
  sketch-geometry (2):
    g0: Circle CenterX=94.4 CenterY=37.5 CenterZ=0 NormalX=0 NormalY=0 NormalZ=1 AngleXU=0 Radius=1.5
    g1: Circle CenterX=94.4 CenterY=37.5 CenterZ=0 NormalX=0 NormalY=0 NormalZ=1 AngleXU=0 Radius=2
  constraints (3):
    c: Coincident(g1,g0)
    c: Radius(g0) = 1.5
    c: Radius(g1) = 2
FEATURE [App::MeasureDistance] Distance  label="Distance: 6,15 mm"
  Distance = 6.14811
  P1 = (1.5,-21.9,3.5e-14)
  P2 = (1.5,-28.0481,3.35e-14)
FEATURE [PartDesign::Body] Body
  Group = -> [Sketch,Sketch001,Sketch002,Sketch003,Pad,Thickness,Sketch004,Pad001,Pad002,Pad003,Fillet,Pad004,Sketch005,Sketch006,Pad005,Sketch007,Pocket,Hole,Sketch010,Pocket001,Sketch011,Sketch012,Sketch013,Pad008,Pocket002,Sketch014,Pocket003,Pocket004,Sketch026,Pad011,Fillet001,Fillet002,Fillet003,Sketch027,Pad012,Sketch028,Sketch029,Pad013,Fillet004,Sketch030,Pad014,Sketch031,Pad015]
  Origin = -> Origin
  Tip = -> Pad015
FEATURE [Sketcher::SketchObject] Sketch014  label="IR-Receiverloch"
  AttachmentOffset = pos=(0,0,0.5) rot=(0,0,1;0rad)
  FullyConstrained = true
  MapMode = 5
  Placement = pos=(-0.5,0,0) rot=(0.57735,-0.57735,-0.57735;2.0944rad)
  Support = -> [Pocket004]
  sketch-geometry (4):
    g0: LineSegment StartX=36 StartY=0 StartZ=0 EndX=36 EndY=3.5 EndZ=0
    g1: LineSegment StartX=36 StartY=3.5 StartZ=0 EndX=30 EndY=3.5 EndZ=0
    g2: LineSegment StartX=30 StartY=3.5 StartZ=0 EndX=30 EndY=0 EndZ=0
    g3: LineSegment StartX=30 StartY=0 StartZ=0 EndX=36 EndY=0 EndZ=0
  constraints (12):
    c: Horizontal(g1)
    c: Coincident(g2,g1)
    c: Vertical(g2)
    c: Coincident(g3,g2)
    c: Coincident(g3,g0)
    c: Vertical(g0)
    c: Coincident(g0,g1)
    c: DistanceX(g3,g3) = 6
    c: DistanceY(g2,g2) = 3.5
    c: PointOnObject(g0,g-1)
    c: Horizontal(g3)
    c: DistanceX(g-1,g2) = 30
FEATURE [PartDesign::Pocket] Pocket004
  BaseFeature = -> Pocket003
  Direction = (1,0,0)
  Length = 5
  Length2 = 5
  Profile = -> Sketch014
  ReferenceAxis = -> Sketch014 [N_Axis]
  Type = 0
FEATURE [PartDesign::Pad] Pad011  label="Triggerbefestigung"
  BaseFeature = -> Pocket004
  Direction = (0,0,-1)
  Length = 13.5
  Length2 = 10
  Profile = -> Sketch026
  ReferenceAxis = -> Sketch026 [N_Axis]
  Type = 0
FEATURE [App::Part] Part
  Group = -> [Body]
  Origin = -> Origin001
FEATURE [PartDesign::Fillet] Fillet001
  Base = -> Pad011 [Edge147,Edge145,Edge139]
  BaseFeature = -> Pad011
  Radius = 1
  SupportTransform = false
  UseAllEdges = false
FEATURE [PartDesign::Fillet] Fillet002
  Base = -> Fillet001 [Edge118]
  BaseFeature = -> Fillet001
  Radius = 5
  SupportTransform = false
  UseAllEdges = false
FEATURE [PartDesign::Fillet] Fillet003
  Base = -> Fillet002 [Edge4,Edge2,Edge1,Edge5,Edge7]
  BaseFeature = -> Fillet002
  Radius = 3
  SupportTransform = false
  UseAllEdges = false
FEATURE [Sketcher::SketchObject] Sketch027
  ExternalGeometry = -> [Fillet003]
  FullyConstrained = true
  MapMode = 5
  Placement = pos=(0,0,17.5) rot=(1,0,0;3.14159rad)
  Support = -> [Fillet003]
  sketch-geometry (4):
    g0: LineSegment StartX=154.28 StartY=115.392 StartZ=0 EndX=170.28 EndY=115.392 EndZ=0
    g1: LineSegment StartX=170.28 StartY=115.392 StartZ=0 EndX=170.28 EndY=107.392 EndZ=0
    g2: LineSegment StartX=170.28 StartY=107.392 StartZ=0 EndX=154.28 EndY=107.392 EndZ=0
    g3: LineSegment StartX=154.28 StartY=107.392 StartZ=0 EndX=154.28 EndY=115.392 EndZ=0
  constraints (10):
    c: Coincident(g0,g1)
    c: Coincident(g1,g2)
    c: Coincident(g2,g3)
    c: Coincident(g3,g0)
    c: Horizontal(g2)
    c: Vertical(g1)
    c: Vertical(g3)
    c: Coincident(g0,g-3)
    c: Coincident(g0,g-4)
    c: DistanceY(g3,g3) = 8
FEATURE [PartDesign::Pad] Pad012
  BaseFeature = -> Fillet003
  Direction = (0,0,-1)
  Length = 14
  Length2 = 10
  Profile = -> Sketch027
  ReferenceAxis = -> Sketch027 [N_Axis]
  Type = 0
FEATURE [Sketcher::SketchObject] Sketch028
  FullyConstrained = true
  MapMode = 5
  Placement = pos=(0,0,17.5) rot=(1,0,0;3.14159rad)
  Support = -> [Pad012]
FEATURE [Sketcher::SketchObject] Sketch029
  ExternalGeometry = -> [Pad012]
  FullyConstrained = true
  MapMode = 5
  Placement = pos=(1.5,0,0) rot=(0.57735,0.57735,0.57735;2.0944rad)
  Support = -> [Pad012]
  sketch-geometry (4):
    g0: LineSegment StartX=-18.4 StartY=4.03e-14 StartZ=0 EndX=-18.4 EndY=17.5 EndZ=0
    g1: LineSegment StartX=-18.4 StartY=17.5 StartZ=0 EndX=-12.4 EndY=17.5 EndZ=0
    g2: LineSegment StartX=-12.4 StartY=17.5 StartZ=0 EndX=-12.4 EndY=2.49e-14 EndZ=0
    g3: ArcOfCircle CenterX=-15.4 CenterY=0 CenterZ=0 NormalX=0 NormalY=0 NormalZ=1 AngleXU=0 Radius=3 StartAngle=7.8e-15 EndAngle=3.14159
  constraints (12):
    c: PointOnObject(g0,g-4)
    c: Coincident(g0,g-3)
    c: Vertical(g0)
    c: PointOnObject(g1,g0)
    c: Horizontal(g1)
    c: Coincident(g2,g1)
    c: Coincident(g2,g-3)
    c: Vertical(g2)
    c: PointOnObject(g1,g-4)
    c: Coincident(g3,g-3)
    c: Coincident(g3,g0)
    c: Coincident(g3,g2)
FEATURE [PartDesign::Pad] Pad013
  BaseFeature = -> Pad012
  Direction = (1,0,0)
  Length = 8
  Length2 = 10
  Profile = -> Sketch029
  ReferenceAxis = -> Sketch029 [N_Axis]
  Type = 0
FEATURE [PartDesign::Fillet] Fillet004
  Base = -> Pad013 [Edge270]
  BaseFeature = -> Pad013
  Radius = 2
  SupportTransform = false
  UseAllEdges = false
FEATURE [Sketcher::SketchObject] Sketch030
  AttachmentOffset = pos=(0,0,7) rot=(0,0,1;0rad)
  ExternalGeometry = -> [Fillet004]
  FullyConstrained = true
  MapMode = 5
  Placement = pos=(8.5,0,0) rot=(0.57735,0.57735,0.57735;2.0944rad)
  Support = -> [Fillet004]
  sketch-geometry (4):
    g0: LineSegment StartX=-9 StartY=17.5 StartZ=0 EndX=-3 EndY=17.5 EndZ=0
    g1: LineSegment StartX=-3 StartY=17.5 StartZ=0 EndX=-3 EndY=3.2e-14 EndZ=0
    g2: LineSegment StartX=-9 StartY=3.77e-14 StartZ=0 EndX=-9 EndY=17.5 EndZ=0
    g3: ArcOfCircle CenterX=-6 CenterY=0 CenterZ=0 NormalX=0 NormalY=0 NormalZ=1 AngleXU=0 Radius=3 StartAngle=1.01e-14 EndAngle=3.14159
  constraints (11):
    c: Coincident(g0,g1)
    c: Coincident(g2,g0)
    c: Horizontal(g0)
    c: Vertical(g1)
    c: Vertical(g2)
    c: Coincident(g1,g-3)
    c: Coincident(g-3,g2)
    c: Coincident(g3,g-3)
    c: Coincident(g3,g2)
    c: Coincident(g3,g1)
    c: PointOnObject(g0,g-4)
FEATURE [PartDesign::Pad] Pad014
  BaseFeature = -> Fillet004
  Direction = (1,0,0)
  Length = 6
  Length2 = 10
  Midplane = true
  Profile = -> Sketch030
  ReferenceAxis = -> Sketch030 [N_Axis]
  Type = 0
FEATURE [Sketcher::SketchObject] Sketch031
  ExternalGeometry = -> [Pad014]
  FullyConstrained = true
  MapMode = 5
  Placement = pos=(0,0,4) rot=(1,0,0;3.14159rad)
  Support = -> [Pad014]
  sketch-geometry (2):
    g0: Circle CenterX=94.4 CenterY=37.5 CenterZ=0 NormalX=0 NormalY=0 NormalZ=1 AngleXU=0 Radius=1.5
    g1: Circle CenterX=94.4 CenterY=37.5 CenterZ=0 NormalX=0 NormalY=0 NormalZ=1 AngleXU=0 Radius=3
  constraints (4):
    c: Coincident(g0,g-4)
    c: Coincident(g1,g0)
    c: Equal(g0,g-3)
    c: Diameter(g1) = 6
FEATURE [PartDesign::Pad] Pad015
  BaseFeature = -> Pad014
  Direction = (0,0,-1)
  Length = 15
  Length2 = 10
  Profile = -> Sketch031
  ReferenceAxis = -> Sketch031 [N_Axis]
  Reversed = true
  Type = 0
